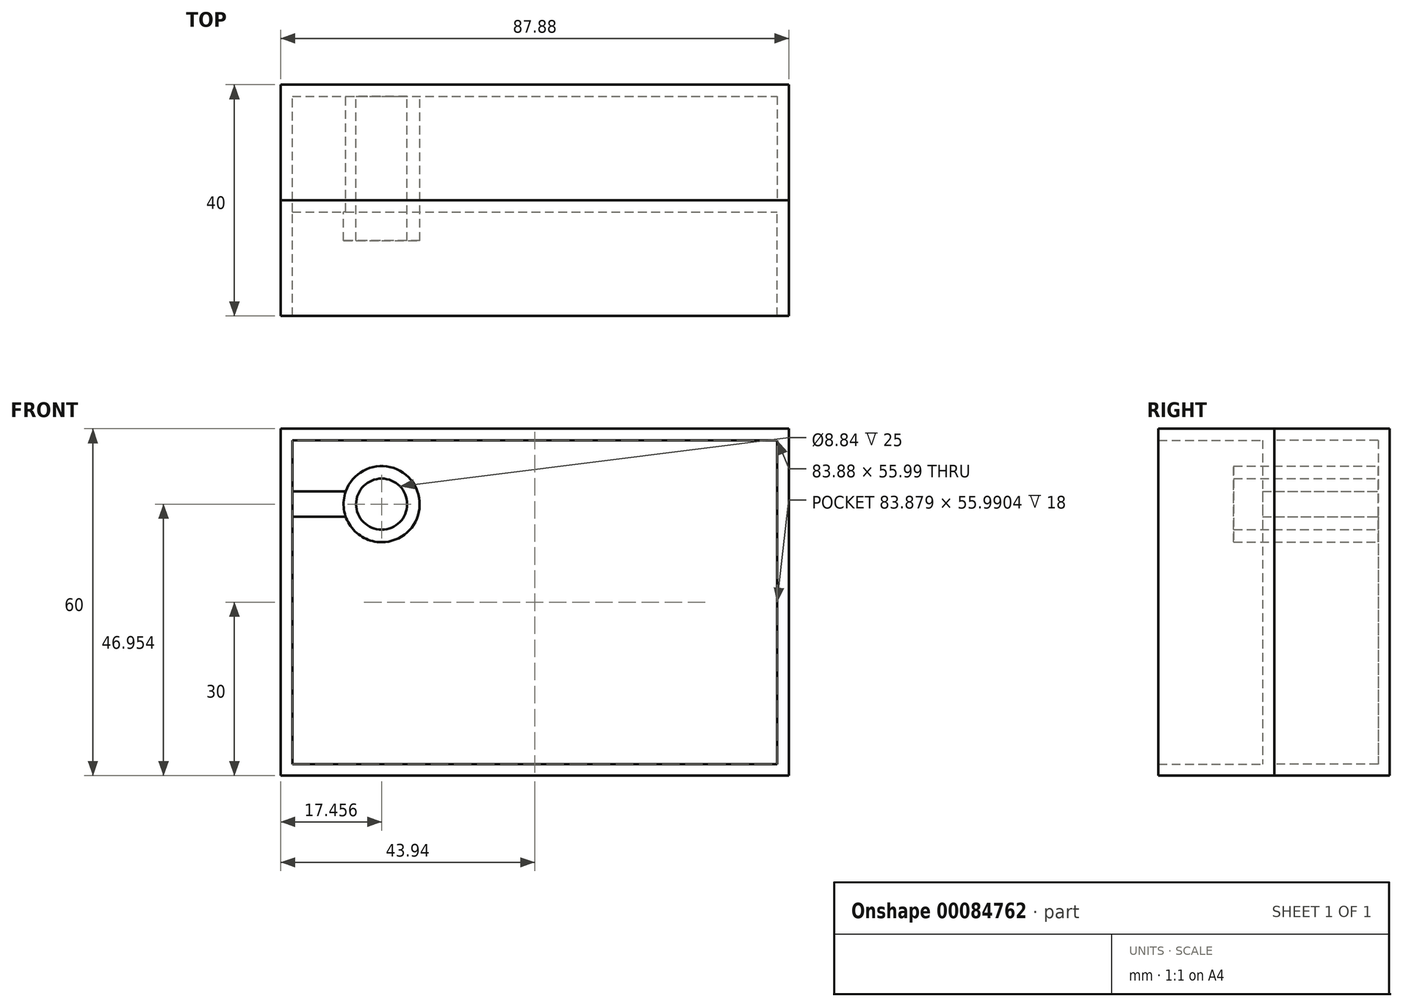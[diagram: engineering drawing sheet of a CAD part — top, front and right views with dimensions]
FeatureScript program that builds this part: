
annotation { "Feature Type Name" : "Feature", "Feature Type Description" : "" }
export const myFeature = defineFeature(function(context is Context, id is Id, definition is map)
    precondition{}
    {
        {
            var Q0;
            Q0=qCreatedBy(makeId("Front.planeOp"),FACE);
            var sketch = newSketch(context, id + "F0", { "sketchPlane" : qUnion([Q0])});
            skLineSegment(sketch, "E0.bottom", {"start": v(-43.94, 30) * mm, "end": v(43.94, 30) * mm});
            skLineSegment(sketch, "E0.top", {"start": v(-43.94, -30) * mm, "end": v(43.94, -30) * mm});
            skLineSegment(sketch, "E0.left", {"start": v(-43.94, 30) * mm, "end": v(-43.94, -30) * mm});
            skLineSegment(sketch, "E0.right", {"start": v(43.94, 30) * mm, "end": v(43.94, -30) * mm});
            skPoint(sketch, "E0.middle", {"position": v(0, 0) * mm});
            skSolve(sketch);
        }
        {
            var Q0;
            Q0=makeQuery(id+"F0.imprint","IMPRINT",FACE,{"disambiguationData":[TD([[makeQuery(id+"F0.imprint","IMPRINT",EDGE,{"derivedFrom":sQuery(id+"F0.wireOp",EDGE,"E0.bottom")}),-1.0]])]});
            extrude(context, id + "F1", {"entities" : qUnion([Q0]), "oppositeDirection" : true, "depth" : 20 * mm});
        }
        {
            var Q0;
            Q0=makeQuery(id+"F1.opExtrude","CAP_FACE",FACE,{"disambiguationData":[OSD([sQuery(id+"F0.wireOp",EDGE,"E0.bottom"),sQuery(id+"F0.wireOp",EDGE,"E0.top"),sQuery(id+"F0.wireOp",EDGE,"E0.left"),sQuery(id+"F0.wireOp",EDGE,"E0.right")])],"isStart":true});
            shell(context, id + "F2", {"entities" : qUnion([Q0]), "thickness" : 2 * mm});
        }
        {
            var Q0;
            Q0=makeQuery(id+"F2.opShell","OFFSET_FACE",FACE,{"disambiguationData":[OSD([sQuery(id+"F0.wireOp",EDGE,"E0.bottom"),sQuery(id+"F0.wireOp",EDGE,"E0.top"),sQuery(id+"F0.wireOp",EDGE,"E0.left"),sQuery(id+"F0.wireOp",EDGE,"E0.right")])]});
            var sketch = newSketch(context, id + "F3", { "sketchPlane" : qUnion([Q0])});
            skCircle(sketch, "E1", {"center": v(-26.48, 16.95) * mm, "radius": 6.58 * mm});
            skCircle(sketch, "E2", {"center": v(-26.48, 16.95) * mm, "radius": 4.42 * mm});
            skLineSegment(sketch, "E3", {"start": v(-41.94, 19.16) * mm, "end": v(-32.68, 19.16) * mm});
            skLineSegment(sketch, "E4", {"start": v(-41.94, 14.75) * mm, "end": v(-32.68, 14.75) * mm});
            skSolve(sketch);
        }
        {
            var Q0;
            Q0 = qSketchRegion(id + "F3", true);
            extrude(context, id + "F4", {"entities" : qUnion([Q0]), "operationType" : NewBodyOperationType.ADD, "depth" : 25 * mm});
        }
        {
            var Q0;
            {var subQ0=sQuery(id+"F3.wireOp",EDGE,"E3");Q0=makeQuery(id+"F3.imprint","IMPRINT",FACE,{"disambiguationData":[TD([[makeQuery(id+"F3.imprint","IMPRINT",EDGE,{"derivedFrom":subQ0}),-1.0]])]});}
            var Q1;
            Q1=sQuery(id+"F3.wireOp",EDGE,"E3");
            var Q2;
            Q2=sQuery(id+"F3.wireOp",EDGE,"E4");
            extrude(context, id + "F5", {"entities" : qUnion([Q0]), "operationType" : NewBodyOperationType.ADD, "surfaceEntities" : qUnion([Q1, Q2]), "depth" : 20 * mm});
        }
        {
            var Q0;
            Q0=qCreatedBy(makeId("Front.planeOp"),FACE);
            var sketch = newSketch(context, id + "F6", { "sketchPlane" : qUnion([Q0])});
            skLineSegment(sketch, "E5.0", {"start": v(-43.94, 30) * mm, "end": v(43.94, 30) * mm});
            skLineSegment(sketch, "E5.1", {"start": v(-43.94, 30) * mm, "end": v(-43.94, -30) * mm});
            skLineSegment(sketch, "E5.2", {"start": v(-43.94, -30) * mm, "end": v(43.94, -30) * mm});
            skLineSegment(sketch, "E5.3", {"start": v(43.94, 30) * mm, "end": v(43.94, -30) * mm});
            skSolve(sketch);
        }
        {
            var Q0;
            Q0=makeQuery(id+"F6.imprint","IMPRINT",FACE,{"disambiguationData":[TD([[makeQuery(id+"F6.imprint","IMPRINT",EDGE,{"derivedFrom":sQuery(id+"F6.wireOp",EDGE,"E5.0")}),-1.0]])]});
            extrude(context, id + "F7", {"entities" : qUnion([Q0]), "depth" : 20 * mm});
        }
        {
            var Q0;
            Q0=makeQuery(id+"F7.opExtrude","CAP_FACE",FACE,{"disambiguationData":[OSD([sQuery(id+"F6.wireOp",EDGE,"E5.0"),sQuery(id+"F6.wireOp",EDGE,"E5.1"),sQuery(id+"F6.wireOp",EDGE,"E5.2"),sQuery(id+"F6.wireOp",EDGE,"E5.3")])],"isStart":false});
            shell(context, id + "F8", {"entities" : qUnion([Q0]), "thickness" : 2 * mm});
        }
    });
